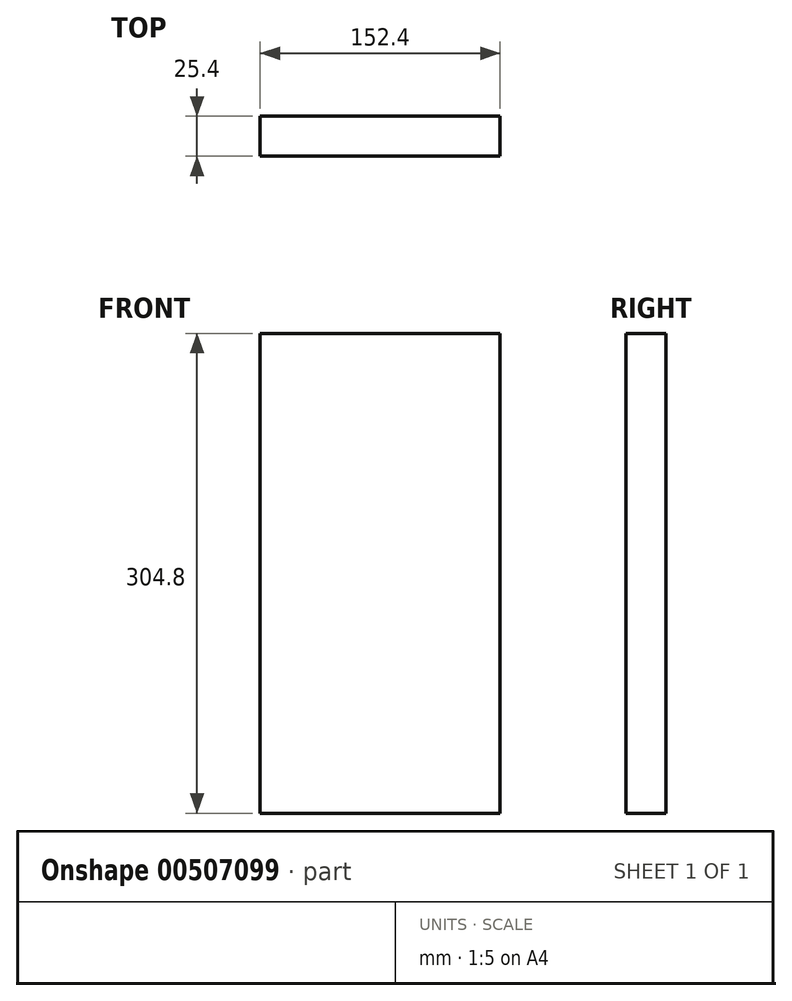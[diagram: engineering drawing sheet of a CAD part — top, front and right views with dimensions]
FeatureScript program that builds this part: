
annotation { "Feature Type Name" : "Feature", "Feature Type Description" : "" }
export const myFeature = defineFeature(function(context is Context, id is Id, definition is map)
    precondition{}
    {
        {
            var Q0;
            Q0=qCreatedBy(makeId("Front.planeOp"),FACE);
            var sketch = newSketch(context, id + "F0", { "sketchPlane" : qUnion([Q0])});
            skLineSegment(sketch, "E0.bottom", {"start": v(-52.52, 155.41) * mm, "end": v(99.88, 155.41) * mm});
            skLineSegment(sketch, "E0.top", {"start": v(-52.52, -149.39) * mm, "end": v(99.88, -149.39) * mm});
            skLineSegment(sketch, "E0.left", {"start": v(-52.52, 155.41) * mm, "end": v(-52.52, -149.39) * mm});
            skLineSegment(sketch, "E0.right", {"start": v(99.88, 155.41) * mm, "end": v(99.88, -149.39) * mm});
            skSolve(sketch);
        }
        {
            var Q0;
            Q0=makeQuery(id+"F0.imprint","IMPRINT",FACE,{"disambiguationData":[TD([[makeQuery(id+"F0.imprint","IMPRINT",EDGE,{"derivedFrom":sQuery(id+"F0.wireOp",EDGE,"E0.bottom")}),-1.0]])]});
            extrude(context, id + "F1", {"entities" : qUnion([Q0]), "depth" : 25.4 * mm});
        }
    });
